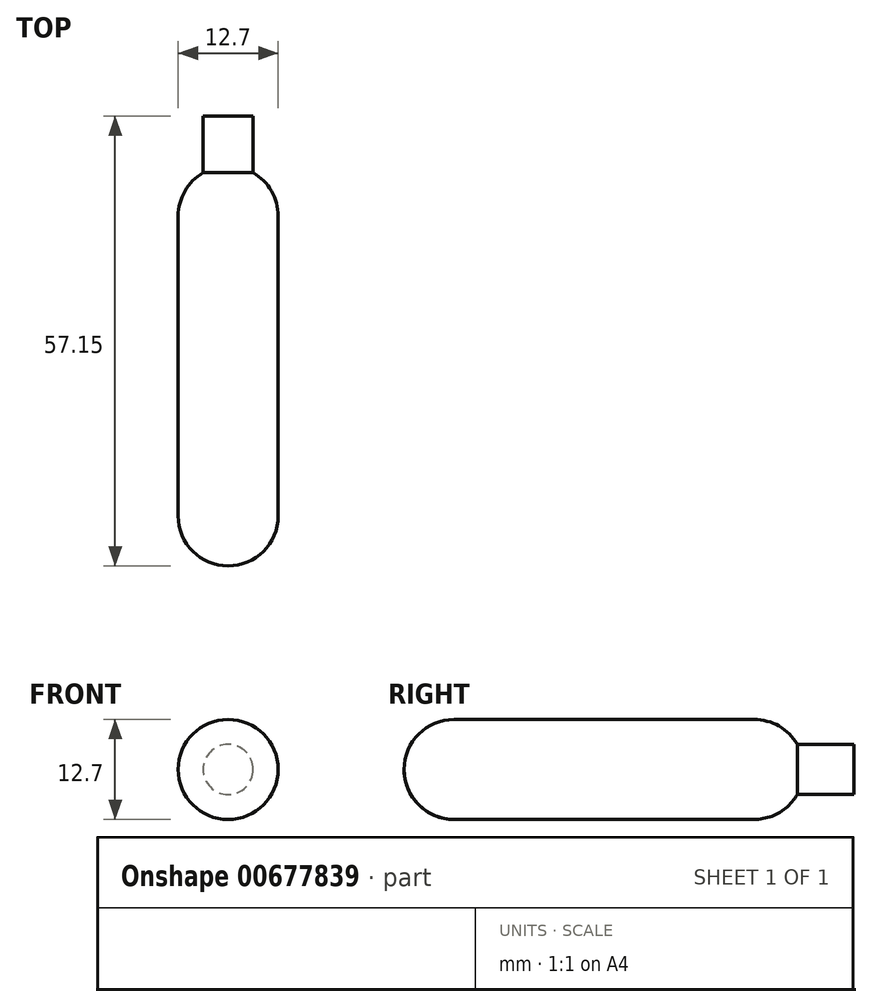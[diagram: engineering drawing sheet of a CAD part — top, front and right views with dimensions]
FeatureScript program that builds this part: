
annotation { "Feature Type Name" : "Feature", "Feature Type Description" : "" }
export const myFeature = defineFeature(function(context is Context, id is Id, definition is map)
    precondition{}
    {
        {
            var Q0;
            Q0=qCreatedBy(makeId("Front.planeOp"),FACE);
            var sketch = newSketch(context, id + "F0", { "sketchPlane" : qUnion([Q0])});
            skCircle(sketch, "E0", {"center": v(0, 0) * mm, "radius": 6.35 * mm});
            skSolve(sketch);
        }
        {
            var Q0;
            Q0=makeQuery(id+"F0.imprint","IMPRINT",FACE,{"disambiguationData":[TD([[makeQuery(id+"F0.imprint","IMPRINT",EDGE,{"derivedFrom":sQuery(id+"F0.wireOp",EDGE,"E0")}),1.0]])]});
            extrude(context, id + "F1", {"entities" : qUnion([Q0]), "depth" : 50.8 * mm, "offsetDistance" : 25.4 * mm});
        }
        {
            var Q0;
            Q0=makeQuery(id+"F1.opExtrude","CAP_FACE",FACE,{"disambiguationData":[OSD([sQuery(id+"F0.wireOp",EDGE,"E0")])],"isStart":false});
            fillet(context, id + "F2", {"entities" : qUnion([Q0]), "radius" : 6.35 * mm, "tangentPropagation" : true, "allowEdgeOverflow" : false});
        }
        {
            var Q0;
            Q0=makeQuery(id+"F1.opExtrude","CAP_FACE",FACE,{"disambiguationData":[OSD([sQuery(id+"F0.wireOp",EDGE,"E0")])],"isStart":true});
            fillet(context, id + "F3", {"entities" : qUnion([Q0]), "radius" : 6.35 * mm, "tangentPropagation" : true, "allowEdgeOverflow" : false});
        }
        {
            var Q0;
            Q0=qCreatedBy(makeId("Front.planeOp"),FACE);
            var sketch = newSketch(context, id + "F4", { "sketchPlane" : qUnion([Q0])});
            skCircle(sketch, "E1", {"center": v(0, 0) * mm, "radius": 3.18 * mm});
            skSolve(sketch);
        }
        {
            var Q0;
            Q0=makeQuery(id+"F4.imprint","IMPRINT",FACE,{"disambiguationData":[TD([[makeQuery(id+"F4.imprint","IMPRINT",EDGE,{"derivedFrom":sQuery(id+"F4.wireOp",EDGE,"E1")}),1.0]])]});
            extrude(context, id + "F5", {"entities" : qUnion([Q0]), "operationType" : NewBodyOperationType.ADD, "endBound" : BoundingType.SYMMETRIC, "depth" : 12.7 * mm, "offsetDistance" : 25.4 * mm});
        }
    });
